# Revit family: Door-Floor_Access-Bilco-Single_Leaf-Fire_Rated
name_source: partatom
category: Doors
units: mm (PartAtom-declared; Revit-internal decimal feet)

## family parameters
Classification Number = 23.30.10.27.17
Cut with Voids When Loaded = No
Host = Face
Room Calculation Point = No
Shared = No

## types (5) — shared parameters
Analytic Construction = <None>
Arm Guide GAP = 1 "
Arm Guide Location = 4.75 "
Cover Material = Aluminum-Bilco-Mill Finish
Cover Opening = 85.00°
Description = Fire Rated Floor Door
Frame Material = Aluminum-Bilco-Mill Finish
Function = Interior
Hardware Material = Zinc Plated-Bilco-Chromate Sealed
Height = 12.594 "
Manufacturer = Bilco
Product Documentation Link = http://www.bilco.com
Product Page URL = https://www.bilco.com
Rough Difference = 3 "
URL = http://www.bilco.com
zero-valued in all types: Default Elevation

## per-type parameters (varying)
| type | Cover Length | Cover Width | Length | Rough Height | Rough Width | Width |
| FR-2 | 34.626 " | 34.626 " | 30 " | 36 " | 36 " | 30 " |
| FR-3 | 34.626 " | 40.626 " | 30 " | 36 " | 42 " | 36 " |
| FR-4 | 40.626 " | 40.626 " | 36 " | 42 " | 42 " | 36 " |
| FR-5 | 46.626 " | 46.626 " | 42 " | 48 " | 48 " | 42 " |
| FR-6 | 52.626 " | 34.626 " | 48 " | 54 " | 36 " | 30 " |

note: column(s) folded — value = type name in every type: Model

## geometry (parser evidence)
native form markers: Blend x4, Sweep x17
no freeform markers — native parametric forms only
